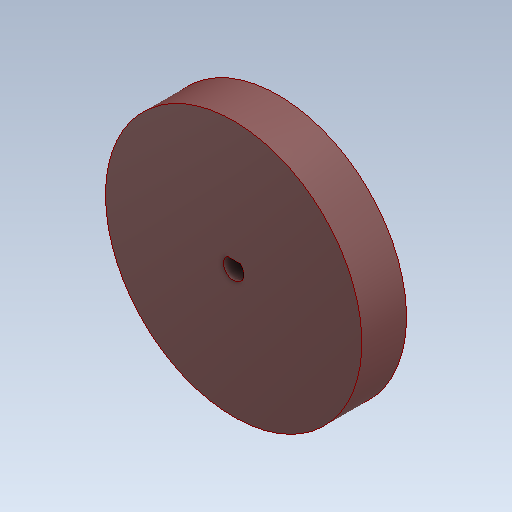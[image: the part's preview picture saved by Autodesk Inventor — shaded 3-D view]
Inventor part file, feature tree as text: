
AUTODESK INVENTOR PART (.ipt)
format: ipt  version: 2020 (Build 240168000, 168)  size: 110,592 bytes
history: native  units: mm
features: other x1, extrude x1, sketch x1, imported_body x1
ambient origin geometry x8: Origin, YZ Plane, XZ Plane, XY Plane, X Axis, Y Axis, Z Axis, Center Point
bodies: Body1 (feature_tree)
feature tree (4):
  other  "Твердое тело1"
  extrude  "Выдавливание1"  Depth=50.0mm
  sketch  "Эскиз1"
  imported_body  "БазТело1"
